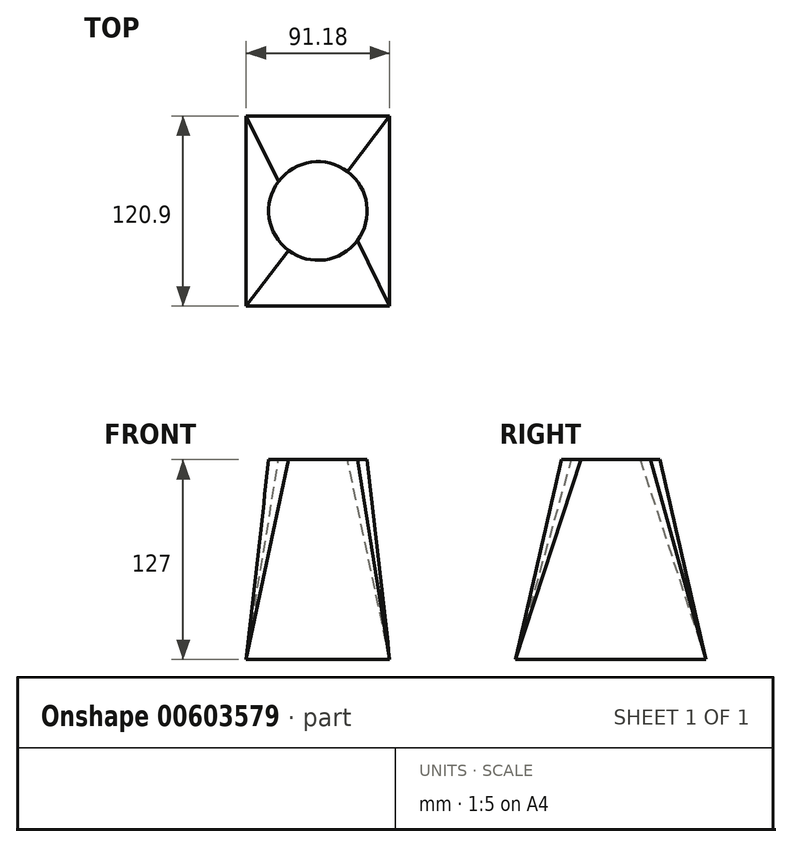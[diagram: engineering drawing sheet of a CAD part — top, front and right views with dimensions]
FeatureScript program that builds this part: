
annotation { "Feature Type Name" : "Feature", "Feature Type Description" : "" }
export const myFeature = defineFeature(function(context is Context, id is Id, definition is map)
    precondition{}
    {
        {
            var Q0;
            Q0=qCreatedBy(makeId("Top.planeOp"),FACE);
            var sketch = newSketch(context, id + "F0", { "sketchPlane" : qUnion([Q0])});
            skLineSegment(sketch, "E0.bottom", {"start": v(45.59, 60.45) * mm, "end": v(-45.59, 60.45) * mm});
            skLineSegment(sketch, "E0.top", {"start": v(45.59, -60.45) * mm, "end": v(-45.59, -60.45) * mm});
            skLineSegment(sketch, "E0.left", {"start": v(45.59, 60.45) * mm, "end": v(45.59, -60.45) * mm});
            skLineSegment(sketch, "E0.right", {"start": v(-45.59, 60.45) * mm, "end": v(-45.59, -60.45) * mm});
            skPoint(sketch, "E0.middle", {"position": v(0, 0) * mm});
            skSolve(sketch);
        }
        {
            var Q0;
            Q0=qCreatedBy(makeId("Top.planeOp"),FACE);
            cPlane(context, id + "F1", {"entities" : qUnion([Q0]), "cplaneType" : CPlaneType.OFFSET, "offset" : 127 * mm, "width" : 152.4 * mm, "height" : 152.4 * mm});
        }
        {
            var Q0;
            Q0=qCreatedBy(id+"F1.planeOp",FACE);
            var sketch = newSketch(context, id + "F2", { "sketchPlane" : qUnion([Q0])});
            skPoint(sketch, "E1.middle", {"position": v(0, 0) * mm});
            skCircle(sketch, "E2", {"center": v(0, 0) * mm, "radius": 31.3 * mm});
            skSolve(sketch);
        }
        {
            var Q0;
            Q0=makeQuery(id+"F0.imprint","IMPRINT",FACE,{"disambiguationData":[TD([[makeQuery(id+"F0.imprint","IMPRINT",EDGE,{"derivedFrom":sQuery(id+"F0.wireOp",EDGE,"E0.bottom")}),1.0]])]});
            var Q1;
            Q1 = qSketchRegion(id + "F2", true);
            loft(context, id + "F3", {"sheetProfilesArray" : [{ "sheetProfileEntities" : qUnion([Q0]) }, { "sheetProfileEntities" : qUnion([Q1]) }]});
        }
    });
